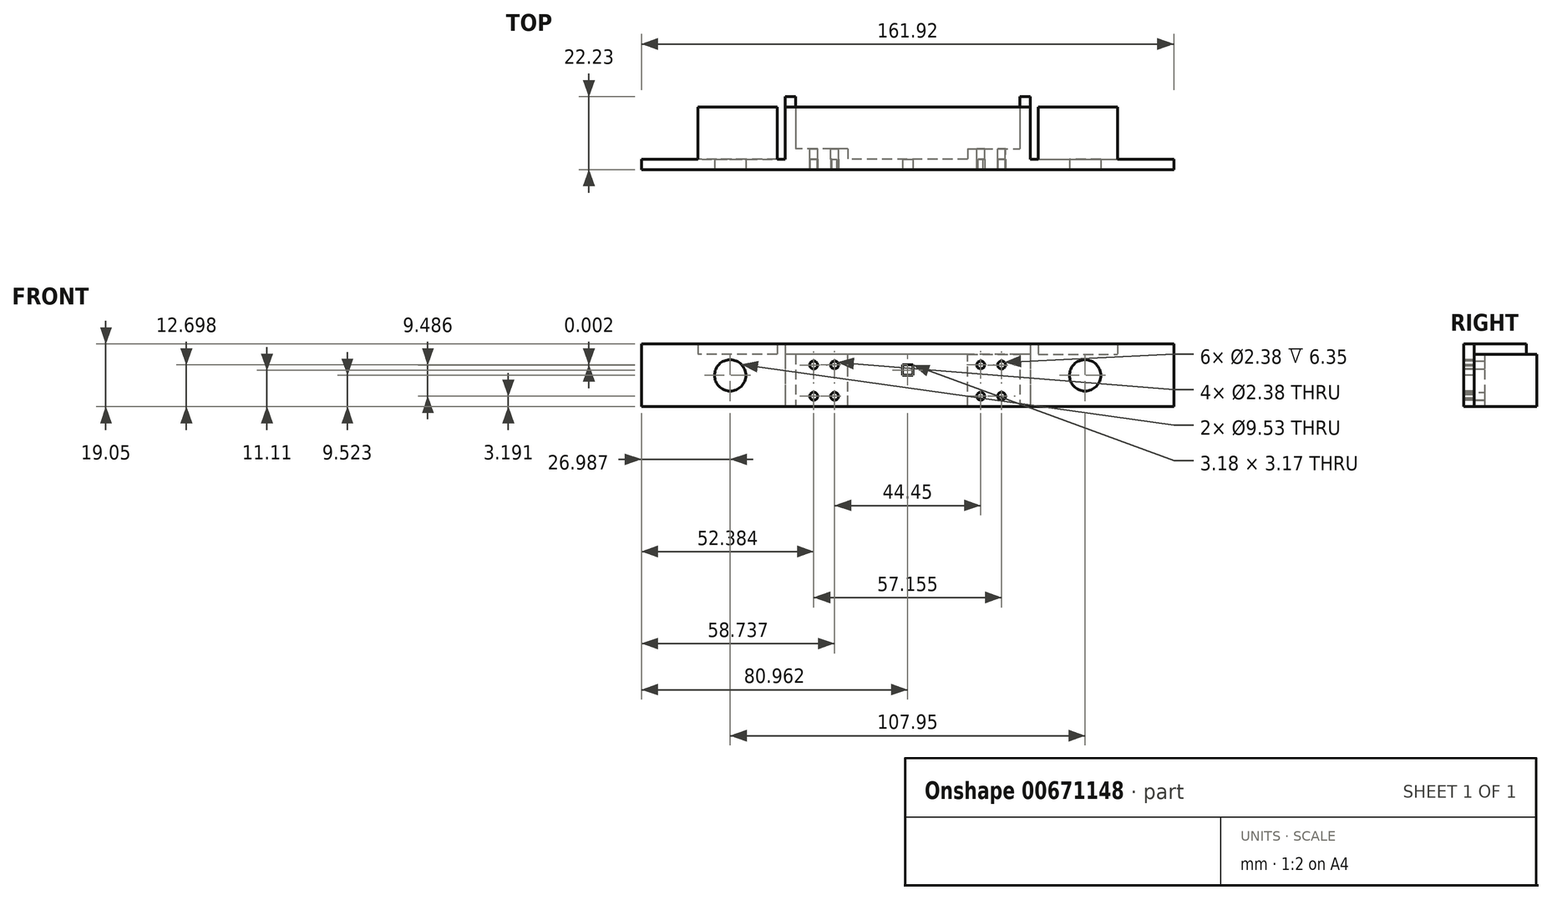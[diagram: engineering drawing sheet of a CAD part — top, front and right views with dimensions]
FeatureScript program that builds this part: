
annotation { "Feature Type Name" : "Feature", "Feature Type Description" : "" }
export const myFeature = defineFeature(function(context is Context, id is Id, definition is map)
    precondition{}
    {
        {
            var Q0;
            Q0=qCreatedBy(makeId("Front.planeOp"),FACE);
            var sketch = newSketch(context, id + "F0", { "sketchPlane" : qUnion([Q0])});
            skLineSegment(sketch, "E0", {"start": v(-49.52, -7.96) * mm, "end": v(112.4, -7.96) * mm});
            skLineSegment(sketch, "E1", {"start": v(112.4, -7.96) * mm, "end": v(112.4, 11.09) * mm});
            skLineSegment(sketch, "E2", {"start": v(112.4, 11.09) * mm, "end": v(-49.52, 11.09) * mm});
            skLineSegment(sketch, "E3", {"start": v(-49.52, 11.09) * mm, "end": v(-49.52, -7.96) * mm});
            skSolve(sketch);
        }
        {
            var Q0;
            Q0=qSketchRegion(id+"F0",true);
            extrude(context, id + "F1", {"entities" : qUnion([Q0]), "depth" : 3.17 * mm});
        }
        {
            var Q0;
            Q0=makeQuery(id+"F1.opExtrude","CAP_FACE",FACE,{"disambiguationData":[OSD([sQuery(id+"F0.wireOp",EDGE,"E0"),sQuery(id+"F0.wireOp",EDGE,"E1"),sQuery(id+"F0.wireOp",EDGE,"E2"),sQuery(id+"F0.wireOp",EDGE,"E3")])],"isStart":false});
            var sketch = newSketch(context, id + "F2", { "sketchPlane" : qUnion([Q0])});
            skCircle(sketch, "E4", {"center": v(-22.53, 1.56) * mm, "radius": 4.76 * mm});
            skCircle(sketch, "E5", {"center": v(2.87, 4.74) * mm, "radius": 1.2 * mm});
            skCircle(sketch, "E6", {"center": v(2.87, -4.79) * mm, "radius": 1.2 * mm});
            skLineSegment(sketch, "E7", {"start": v(31.44, 11.09) * mm, "end": v(31.44, -7.96) * mm});
            skPoint(sketch, "E8.oppositeSnap0", {"position": v(31.44, 1.56) * mm});
            skLineSegment(sketch, "E8.bottom", {"start": v(29.85, 4.74) * mm, "end": v(33.03, 4.74) * mm});
            skLineSegment(sketch, "E8.top", {"start": v(29.85, 1.56) * mm, "end": v(33.03, 1.56) * mm});
            skLineSegment(sketch, "E8.left", {"start": v(29.85, 4.74) * mm, "end": v(29.85, 1.56) * mm});
            skLineSegment(sketch, "E8.right", {"start": v(33.03, 4.74) * mm, "end": v(33.03, 1.56) * mm});
            skCircle(sketch, "E9.MirrorC", {"center": v(85.42, 1.56) * mm, "radius": 4.76 * mm});
            skCircle(sketch, "E10", {"center": v(9.22, 4.74) * mm, "radius": 1.2 * mm});
            skCircle(sketch, "E11", {"center": v(9.22, -4.79) * mm, "radius": 1.2 * mm});
            skCircle(sketch, "E12.MirrorC", {"center": v(53.67, -4.79) * mm, "radius": 1.2 * mm});
            skCircle(sketch, "E13.MirrorC", {"center": v(53.67, 4.74) * mm, "radius": 1.2 * mm});
            skCircle(sketch, "E14.MirrorC", {"center": v(60.02, 4.74) * mm, "radius": 1.2 * mm});
            skCircle(sketch, "E15.MirrorC", {"center": v(60.02, -4.79) * mm, "radius": 1.2 * mm});
            skSolve(sketch);
        }
        {
            var Q0;
            Q0=qSketchRegion(id+"F2",true);
            extrude(context, id + "F3", {"entities" : qUnion([Q0]), "operationType" : NewBodyOperationType.REMOVE, "oppositeDirection" : true, "depth" : 6.35 * mm});
        }
        {
            var Q0;
            Q0=makeQuery(id+"F1.opExtrude","CAP_FACE",FACE,{"disambiguationData":[OSD([sQuery(id+"F0.wireOp",EDGE,"E0"),sQuery(id+"F0.wireOp",EDGE,"E1"),sQuery(id+"F0.wireOp",EDGE,"E2"),sQuery(id+"F0.wireOp",EDGE,"E3")])],"isStart":true});
            var sketch = newSketch(context, id + "F4", { "sketchPlane" : qUnion([Q0])});
            skLineSegment(sketch, "E16", {"start": v(-95.26, 11.09) * mm, "end": v(-95.26, 7.91) * mm});
            skLineSegment(sketch, "E17", {"start": v(32.38, 11.09) * mm, "end": v(32.38, 7.91) * mm});
            skLineSegment(sketch, "E18", {"start": v(5.86, 11.09) * mm, "end": v(5.86, 7.91) * mm});
            skLineSegment(sketch, "E19", {"start": v(-68.75, 11.09) * mm, "end": v(-68.75, 7.91) * mm});
            skLineSegment(sketch, "E20", {"start": v(-68.75, 7.91) * mm, "end": v(5.86, 7.91) * mm});
            skLineSegment(sketch, "E21", {"start": v(-71.13, 11.09) * mm, "end": v(-71.13, 7.91) * mm});
            skLineSegment(sketch, "E22", {"start": v(-71.13, 7.91) * mm, "end": v(-95.26, 7.91) * mm});
            skLineSegment(sketch, "E23", {"start": v(8.25, 11.09) * mm, "end": v(8.25, 7.91) * mm});
            skLineSegment(sketch, "E24", {"start": v(8.25, 7.91) * mm, "end": v(32.38, 7.91) * mm});
            skLineSegment(sketch, "E25", {"start": v(-49.7, 7.91) * mm, "end": v(-49.7, -7.96) * mm});
            skLineSegment(sketch, "E26", {"start": v(-13.19, 7.91) * mm, "end": v(-13.19, -7.96) * mm});
            skLineSegment(sketch, "E27", {"start": v(-68.75, 7.91) * mm, "end": v(-68.75, -7.96) * mm});
            skLineSegment(sketch, "E28", {"start": v(-68.75, -7.96) * mm, "end": v(-65.57, -7.96) * mm});
            skLineSegment(sketch, "E29", {"start": v(-65.57, -7.96) * mm, "end": v(-65.57, 7.91) * mm});
            skLineSegment(sketch, "E30", {"start": v(5.86, 7.91) * mm, "end": v(5.86, -7.96) * mm});
            skLineSegment(sketch, "E31", {"start": v(5.86, -7.96) * mm, "end": v(2.69, -7.96) * mm});
            skLineSegment(sketch, "E32", {"start": v(2.69, -7.96) * mm, "end": v(2.69, 7.91) * mm});
            skSolve(sketch);
        }
        {
            var Q0;
            Q0=qSketchRegion(id+"F2",true);
            extrude(context, id + "F5", {"entities" : qUnion([Q0]), "operationType" : NewBodyOperationType.REMOVE, "oppositeDirection" : true, "depth" : 25.4 * mm});
        }
        {
            var Q0;
            {var subQ0=sQuery(id+"F4.wireOp",EDGE,"E27");Q0=makeQuery(id+"F4.imprint","IMPRINT",FACE,{"disambiguationData":[TD([[makeQuery(id+"F4.imprint","IMPRINT",EDGE,{"derivedFrom":subQ0}),1.0]])]});}
            var Q1;
            {var subQ0=sQuery(id+"F4.wireOp",EDGE,"E30");Q1=makeQuery(id+"F4.imprint","IMPRINT",FACE,{"disambiguationData":[TD([[makeQuery(id+"F4.imprint","IMPRINT",EDGE,{"derivedFrom":subQ0}),-1.0]])]});}
            extrude(context, id + "F6", {"entities" : qUnion([Q0, Q1]), "operationType" : NewBodyOperationType.ADD, "depth" : 19.05 * mm});
        }
        {
            var Q0;
            Q0=makeQuery(id+"F6.opExtrude","SWEPT_FACE",FACE,{"disambiguationData":[OSD([sQuery(id+"F4.wireOp",EDGE,"E29")])]});
            var sketch = newSketch(context, id + "F7", { "sketchPlane" : qUnion([Q0])});
            skLineSegment(sketch, "E33", {"start": v(-3.18, 7.91) * mm, "end": v(-3.17, -7.96) * mm});
            skSolve(sketch);
        }
        {
            var Q0;
            Q0=qSketchRegion(id+"F7",true);
            var Q1;
            {var subQ0=sQuery(id+"F7.wireOp",EDGE,"E33");Q1=makeQuery(id+"F7.imprint","IMPRINT",FACE,{"disambiguationData":[TD([[makeQuery(id+"F7.imprint","IMPRINT",EDGE,{"derivedFrom":subQ0}),1.0]])]});}
            extrude(context, id + "F8", {"entities" : qUnion([Q0, Q1]), "operationType" : NewBodyOperationType.ADD, "depth" : 15.88 * mm});
        }
        {
            var Q0;
            Q0=makeQuery(id+"F6.opExtrude","SWEPT_FACE",FACE,{"disambiguationData":[OSD([sQuery(id+"F4.wireOp",EDGE,"E32")])]});
            var sketch = newSketch(context, id + "F9", { "sketchPlane" : qUnion([Q0])});
            skLineSegment(sketch, "E34", {"start": v(3.17, 7.91) * mm, "end": v(3.18, -7.96) * mm});
            skSolve(sketch);
        }
        {
            var Q0;
            Q0=qSketchRegion(id+"F9",true);
            var Q1;
            {var subQ0=sQuery(id+"F9.wireOp",EDGE,"E34");Q1=makeQuery(id+"F9.imprint","IMPRINT",FACE,{"disambiguationData":[TD([[makeQuery(id+"F9.imprint","IMPRINT",EDGE,{"derivedFrom":subQ0}),-1.0]])]});}
            extrude(context, id + "F10", {"entities" : qUnion([Q0, Q1]), "operationType" : NewBodyOperationType.ADD, "depth" : 15.88 * mm});
        }
        {
            var Q0;
            Q0=qSketchRegion(id+"F4",true);
            var Q1;
            {var subQ0=sQuery(id+"F4.wireOp",EDGE,"E16");Q1=makeQuery(id+"F4.imprint","IMPRINT",FACE,{"disambiguationData":[TD([[makeQuery(id+"F4.imprint","IMPRINT",EDGE,{"derivedFrom":subQ0}),1.0]])]});}
            var Q2;
            {var subQ5=sQuery(id+"F4.wireOp",EDGE,"E18");Q2=makeQuery(id+"F4.imprint","IMPRINT",FACE,{"disambiguationData":[TD([[makeQuery(id+"F4.imprint","IMPRINT",EDGE,{"derivedFrom":subQ5}),-1.0]])]});}
            var Q3;
            {var subQ0=sQuery(id+"F4.wireOp",EDGE,"E17");Q3=makeQuery(id+"F4.imprint","IMPRINT",FACE,{"disambiguationData":[TD([[makeQuery(id+"F4.imprint","IMPRINT",EDGE,{"derivedFrom":subQ0}),-1.0]])]});}
            extrude(context, id + "F11", {"entities" : qUnion([Q0, Q1, Q2, Q3]), "operationType" : NewBodyOperationType.ADD, "depth" : 15.88 * mm});
        }
        {
            var Q0;
            Q0=makeQuery(id+"F10.opExtrude","SWEPT_FACE",FACE,{"disambiguationData":[OSD([sQuery(id+"F9.wireOp",EDGE,"E34")])]});
            var sketch = newSketch(context, id + "F12", { "sketchPlane" : qUnion([Q0])});
            skCircle(sketch, "E35", {"center": v(-9.22, 4.74) * mm, "radius": 1.2 * mm});
            skCircle(sketch, "E36", {"center": v(-9.24, -4.77) * mm, "radius": 1.2 * mm});
            skCircle(sketch, "E37", {"center": v(-2.89, -4.74) * mm, "radius": 1.2 * mm});
            skCircle(sketch, "E38", {"center": v(-2.86, 4.72) * mm, "radius": 1.2 * mm});
            skCircle(sketch, "E39.MirrorC", {"center": v(-53.66, 4.74) * mm, "radius": 1.2 * mm});
            skCircle(sketch, "E40.MirrorC", {"center": v(-60.02, 4.72) * mm, "radius": 1.2 * mm});
            skCircle(sketch, "E41.MirrorC", {"center": v(-53.64, -4.77) * mm, "radius": 1.2 * mm});
            skCircle(sketch, "E42.MirrorC", {"center": v(-60, -4.74) * mm, "radius": 1.2 * mm});
            skSolve(sketch);
        }
        {
            var Q0;
            Q0=qSketchRegion(id+"F12",true);
            extrude(context, id + "F13", {"entities" : qUnion([Q0]), "operationType" : NewBodyOperationType.REMOVE, "oppositeDirection" : true, "depth" : 25.4 * mm});
        }
    });
